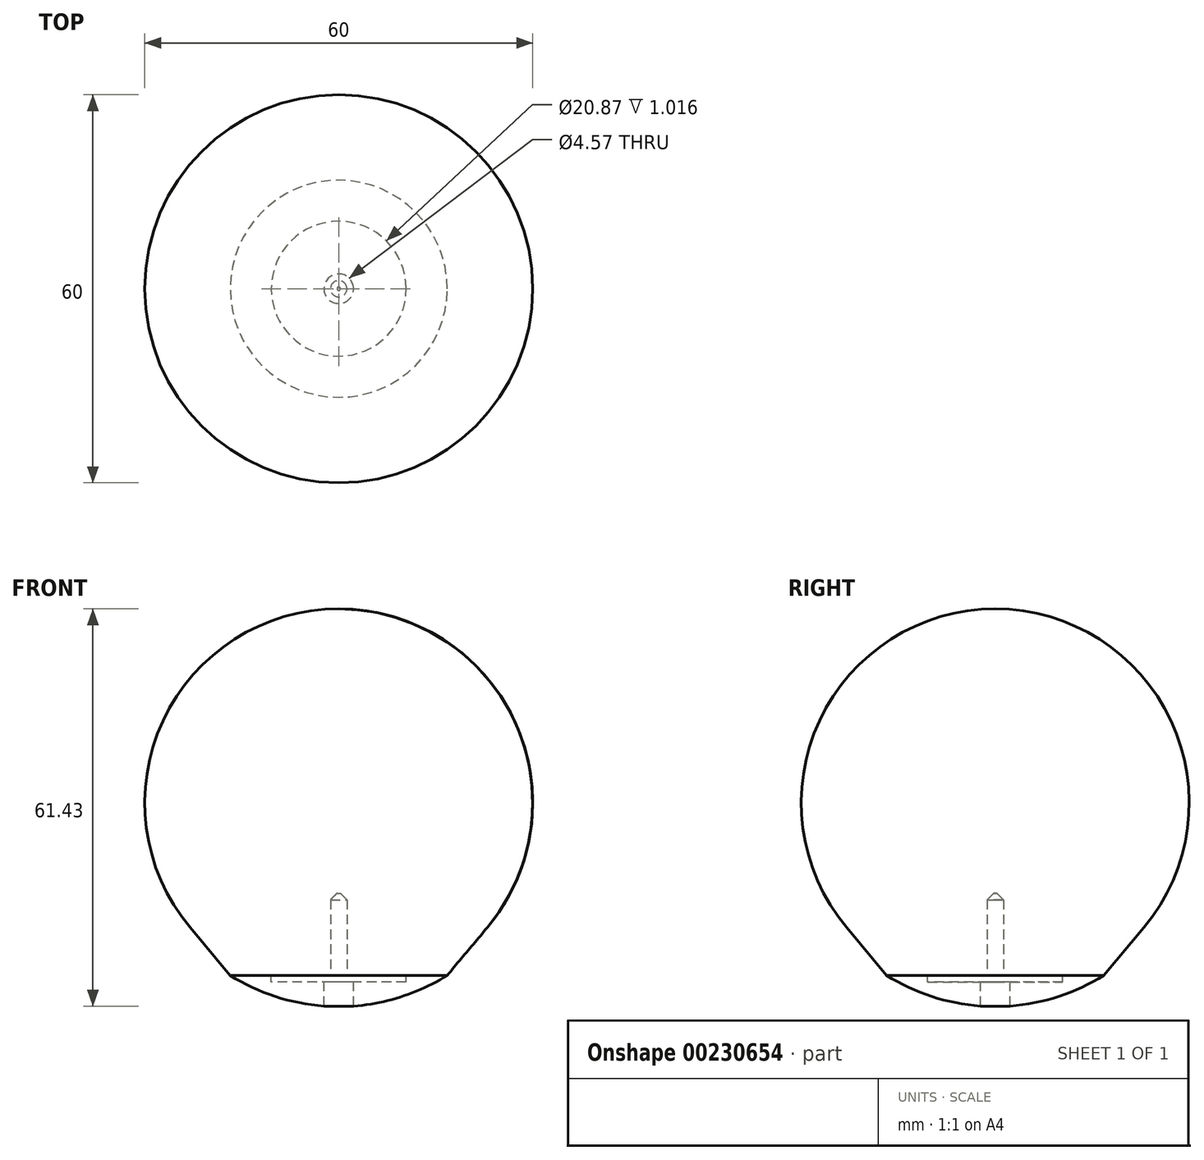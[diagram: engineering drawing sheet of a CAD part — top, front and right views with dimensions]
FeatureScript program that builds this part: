
annotation { "Feature Type Name" : "Feature", "Feature Type Description" : "" }
export const myFeature = defineFeature(function(context is Context, id is Id, definition is map)
    precondition{}
    {
        {
            var Q0;
            Q0=qCreatedBy(makeId("Front.planeOp"),FACE);
            var sketch = newSketch(context, id + "F0", { "sketchPlane" : qUnion([Q0])});
            skArc(sketch, "E0", {"start": v(22.98, 7.39) * mm, "mid": v(27.19, 39.35) * mm, "end": v(0, 56.67) * mm});
            skLineSegment(sketch, "E1", {"start": v(0, 56.67) * mm, "end": v(0, 0) * mm});
            skLineSegment(sketch, "E2", {"start": v(0, 0) * mm, "end": v(16.78, 0) * mm});
            skLineSegment(sketch, "E3", {"start": v(0, 0) * mm, "end": v(0, -57.5) * mm, "construction": true});
            skLineSegment(sketch, "E4", {"start": v(22.98, 7.39) * mm, "end": v(16.78, 0) * mm});
            skSolve(sketch);
        }
        {
            var Q0;
            Q0=makeQuery(id+"F0.imprint","IMPRINT",FACE,{"disambiguationData":[TD([[makeQuery(id+"F0.imprint","IMPRINT",EDGE,{"derivedFrom":sQuery(id+"F0.wireOp",EDGE,"E0")}),1.0]])]});
            var Q1;
            Q1=makeQuery(id+"F0.imprint","IMPRINT",FACE,{"disambiguationData":[TD([[makeQuery(id+"F0.imprint","IMPRINT",EDGE,{"derivedFrom":sQuery(id+"F0.wireOp",EDGE,"zD26rq4C-BGaq-DZ5s-2ClJ-7ZjIpKr6ZtHp")}),1.0]])]});
            var Q2;
            Q2=sQuery(id+"F0.wireOp",EDGE,"E3");
            revolve(context, id + "F1", {"entities" : qUnion([Q0, Q1]), "axis" : qUnion([Q2]), "revolveType" : RevolveType.FULL});
        }
        {
            var Q0;
            Q0=makeQuery(id+"F1.opRevolve","SWEPT_FACE",FACE,{"disambiguationData":[OSD([sQuery(id+"F0.wireOp",EDGE,"E2")])]});
            var sketch = newSketch(context, id + "F2", { "sketchPlane" : qUnion([Q0])});
            skCircle(sketch, "E5", {"center": v(0, 0) * mm, "radius": 1.27 * mm});
            skSolve(sketch);
        }
        {
            var Q0;
            Q0=qSketchRegion(id+"F2",true);
            extrude(context, id + "F3", {"entities" : qUnion([Q0]), "operationType" : NewBodyOperationType.REMOVE, "oppositeDirection" : true, "depth" : 12.7 * mm});
        }
        {
            var Q0;
            Q0=makeQuery(id+"F3.boolean.opBoolean","COPY",EDGE,{"derivedFrom":makeQuery(id+"F3.opExtrude","CAP_EDGE",EDGE,{"disambiguationData":[OSD([sQuery(id+"F2.wireOp",EDGE,"E5")])],"isStart":false})});
            chamfer(context, id + "F4", {"entities" : qUnion([Q0]), "width" : 1.02 * mm, "tangentPropagation" : true});
        }
        {
            var Q0;
            Q0=qCreatedBy(makeId("Front.planeOp"),FACE);
            var sketch = newSketch(context, id + "F5", { "sketchPlane" : qUnion([Q0])});
            skArc(sketch, "E6", {"start": v(0, -4.84) * mm, "mid": v(8.73, -3.6) * mm, "end": v(16.78, 0) * mm});
            skLineSegment(sketch, "E7", {"start": v(16.78, 0) * mm, "end": v(10.43, 0) * mm});
            skLineSegment(sketch, "E8", {"start": v(10.43, 0) * mm, "end": v(10.43, -1.02) * mm});
            skLineSegment(sketch, "E9", {"start": v(10.43, -1.02) * mm, "end": v(0, -1.02) * mm});
            skLineSegment(sketch, "E10", {"start": v(0, -1.02) * mm, "end": v(0, -4.84) * mm});
            skSolve(sketch);
        }
        {
            var Q0;
            Q0=qSketchRegion(id+"F5",true);
            var Q1;
            Q1=sQuery(id+"F0.wireOp",EDGE,"E3");
            revolve(context, id + "F6", {"entities" : qUnion([Q0]), "axis" : qUnion([Q1]), "revolveType" : RevolveType.FULL});
        }
        {
            var Q0;
            Q0=makeQuery(id+"F6.opRevolve","SWEPT_FACE",FACE,{"disambiguationData":[OSD([sQuery(id+"F5.wireOp",EDGE,"E9")])]});
            var sketch = newSketch(context, id + "F7", { "sketchPlane" : qUnion([Q0])});
            skCircle(sketch, "E11", {"center": v(0, 0) * mm, "radius": 2.29 * mm});
            skSolve(sketch);
        }
        {
            var Q0;
            Q0=qSketchRegion(id+"F7",true);
            extrude(context, id + "F8", {"entities" : qUnion([Q0]), "operationType" : NewBodyOperationType.REMOVE, "oppositeDirection" : true, "depth" : 25.4 * mm});
        }
    });
